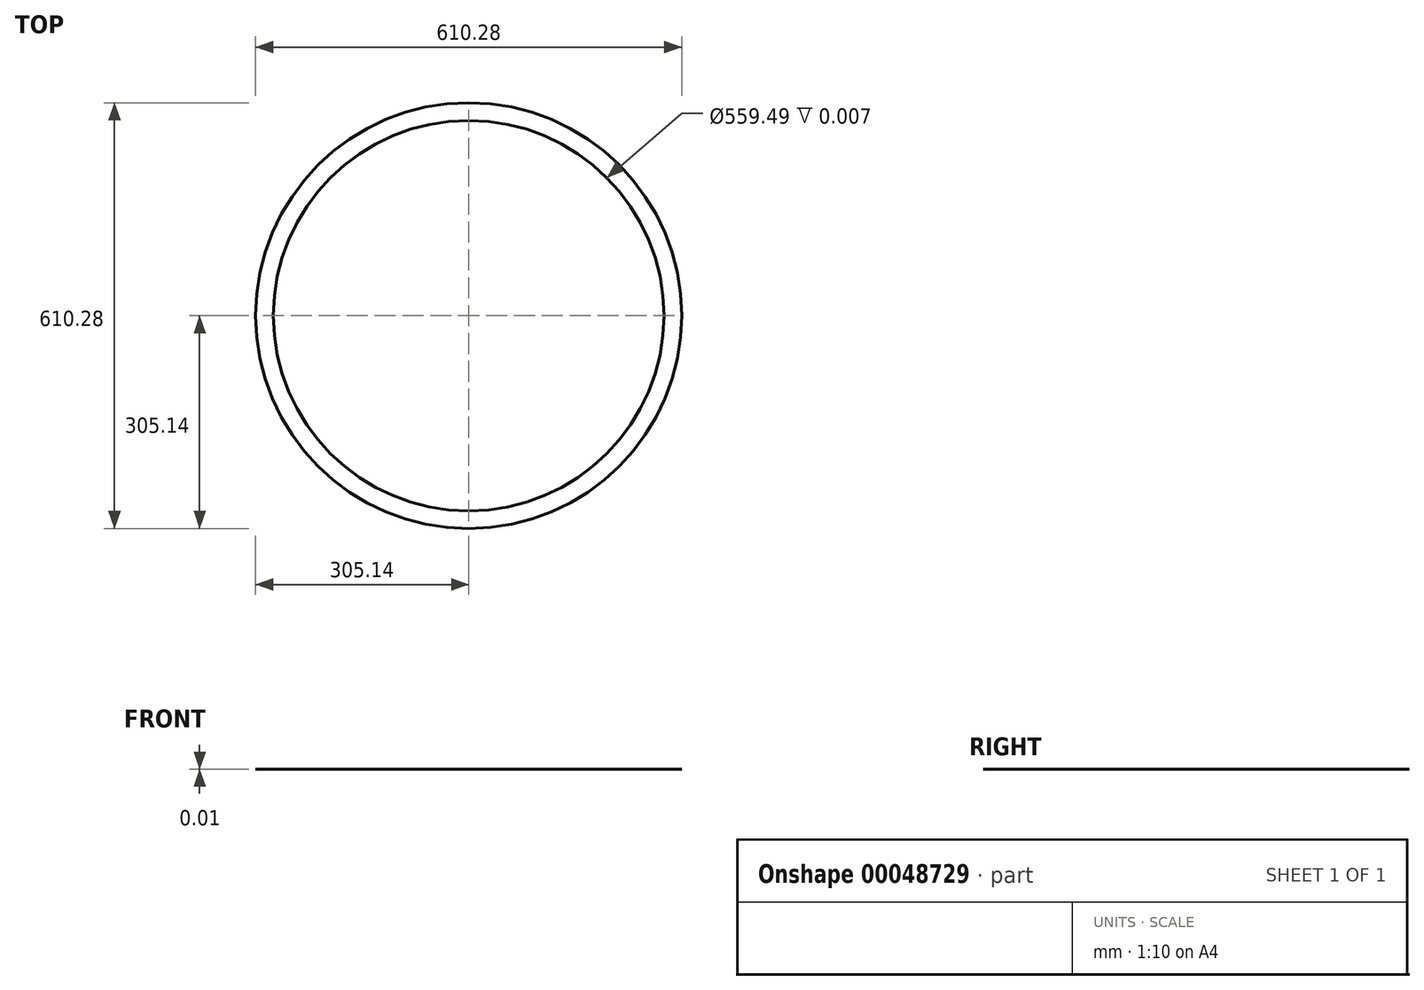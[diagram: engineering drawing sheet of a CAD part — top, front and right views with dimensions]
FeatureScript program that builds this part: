
annotation { "Feature Type Name" : "Feature", "Feature Type Description" : "" }
export const myFeature = defineFeature(function(context is Context, id is Id, definition is map)
    precondition{}
    {
        {
            var Q0;
            Q0=qCreatedBy(makeId("Top.planeOp"),FACE);
            var sketch = newSketch(context, id + "F0", { "sketchPlane" : qUnion([Q0])});
            skCircle(sketch, "E0", {"center": v(0, 0) * mm, "radius": 305.14 * mm});
            skCircle(sketch, "E1", {"center": v(0, 0) * mm, "radius": 279.74 * mm});
            skSolve(sketch);
        }
        {
            var Q0;
            Q0=makeQuery(id+"F0.imprint","IMPRINT",FACE,{"disambiguationData":[TD([[makeQuery(id+"F0.imprint","IMPRINT",EDGE,{"derivedFrom":sQuery(id+"F0.wireOp",EDGE,"E0")}),1.0]])]});
            extrude(context, id + "F1", {"entities" : qUnion([Q0]), "depth" : 3 / 406.4 * mm});
        }
    });
